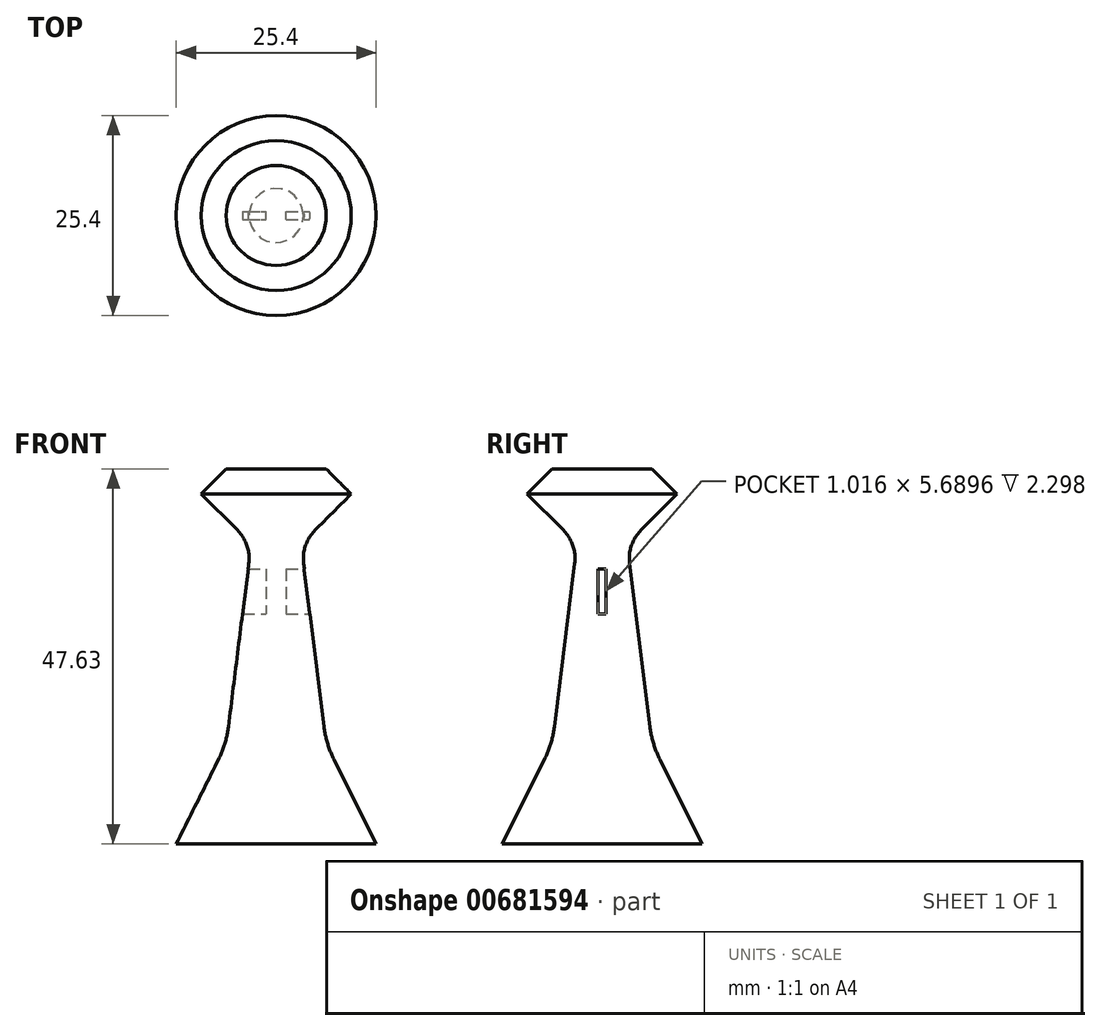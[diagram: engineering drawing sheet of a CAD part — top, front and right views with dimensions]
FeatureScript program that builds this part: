
annotation { "Feature Type Name" : "Feature", "Feature Type Description" : "" }
export const myFeature = defineFeature(function(context is Context, id is Id, definition is map)
    precondition{}
    {
        {
            var Q0;
            Q0=qCreatedBy(makeId("Top.planeOp"),FACE);
            var sketch = newSketch(context, id + "F0", { "sketchPlane" : qUnion([Q0])});
            skCircle(sketch, "E0", {"center": v(0, 0) * mm, "radius": 12.7 * mm});
            skSolve(sketch);
        }
        {
            var Q0;
            Q0=qCreatedBy(makeId("Top.planeOp"),FACE);
            cPlane(context, id + "F1", {"entities" : qUnion([Q0]), "cplaneType" : CPlaneType.OFFSET, "offset" : 12.7 * mm, "width" : 152.4 * mm, "height" : 152.4 * mm});
        }
        {
            var Q0;
            Q0=qCreatedBy(id+"F1.planeOp",FACE);
            var sketch = newSketch(context, id + "F2", { "sketchPlane" : qUnion([Q0])});
            skCircle(sketch, "E1", {"center": v(0, 0) * mm, "radius": 6.35 * mm});
            skSolve(sketch);
        }
        {
            var Q0;
            Q0=makeQuery(id+"F0.imprint","IMPRINT",FACE,{"disambiguationData":[TD([[makeQuery(id+"F0.imprint","IMPRINT",EDGE,{"derivedFrom":sQuery(id+"F0.wireOp",EDGE,"E0")}),1.0]])]});
            var Q1;
            Q1=makeQuery(id+"F2.imprint","IMPRINT",FACE,{"disambiguationData":[TD([[makeQuery(id+"F2.imprint","IMPRINT",EDGE,{"derivedFrom":sQuery(id+"F2.wireOp",EDGE,"E1")}),1.0]])]});
            loft(context, id + "F3", {"sheetProfilesArray" : [{ "sheetProfileEntities" : qUnion([Q0]) }, { "sheetProfileEntities" : qUnion([Q1]) }]});
        }
        {
            var Q0;
            Q0=qCreatedBy(makeId("Top.planeOp"),FACE);
            cPlane(context, id + "F4", {"entities" : qUnion([Q0]), "cplaneType" : CPlaneType.OFFSET, "offset" : 38.1 * mm, "width" : 152.4 * mm, "height" : 152.4 * mm});
        }
        {
            var Q0;
            Q0=qCreatedBy(id+"F4.planeOp",FACE);
            var sketch = newSketch(context, id + "F5", { "sketchPlane" : qUnion([Q0])});
            skCircle(sketch, "E2", {"center": v(0, 0) * mm, "radius": 3.18 * mm});
            skSolve(sketch);
        }
        {
            var Q1;
            Q1=makeQuery(id+"F3.opLoft","CAP_FACE",FACE,{"disambiguationData":[OSD([makeQuery(id+"F2.imprint","IMPRINT",FACE,{"disambiguationData":[TD([[makeQuery(id+"F2.imprint","IMPRINT",EDGE,{"derivedFrom":sQuery(id+"F2.wireOp",EDGE,"E1")}),1.0]])]})])],"isStart":true});
            var Q2;
            Q2=makeQuery(id+"F5.imprint","IMPRINT",FACE,{"disambiguationData":[TD([[makeQuery(id+"F5.imprint","IMPRINT",EDGE,{"derivedFrom":sQuery(id+"F5.wireOp",EDGE,"E2")}),1.0]])]});
            loft(context, id + "F6", {"operationType" : NewBodyOperationType.ADD, "sheetProfilesArray" : [{ "sheetProfileEntities" : qUnion([Q1]) }, { "sheetProfileEntities" : qUnion([Q2]) }]});
        }
        {
            var Q0;
            Q0=qCreatedBy(makeId("Top.planeOp"),FACE);
            cPlane(context, id + "F7", {"entities" : qUnion([Q0]), "cplaneType" : CPlaneType.OFFSET, "offset" : 44.45 * mm, "width" : 152.4 * mm, "height" : 152.4 * mm});
        }
        {
            var Q0;
            Q0=qCreatedBy(id+"F7.planeOp",FACE);
            var sketch = newSketch(context, id + "F8", { "sketchPlane" : qUnion([Q0])});
            skCircle(sketch, "E3", {"center": v(0, 0) * mm, "radius": 9.53 * mm});
            skSolve(sketch);
        }
        {
            var Q1;
            Q1=makeQuery(id+"F6.opLoft","CAP_FACE",FACE,{"disambiguationData":[OSD([makeQuery(id+"F5.imprint","IMPRINT",FACE,{"disambiguationData":[TD([[makeQuery(id+"F5.imprint","IMPRINT",EDGE,{"derivedFrom":sQuery(id+"F5.wireOp",EDGE,"E2")}),1.0]])]})])],"isStart":true});
            var Q2;
            Q2=makeQuery(id+"F8.imprint","IMPRINT",FACE,{"disambiguationData":[TD([[makeQuery(id+"F8.imprint","IMPRINT",EDGE,{"derivedFrom":sQuery(id+"F8.wireOp",EDGE,"E3")}),1.0]])]});
            loft(context, id + "F9", {"operationType" : NewBodyOperationType.ADD, "sheetProfilesArray" : [{ "sheetProfileEntities" : qUnion([Q1]) }, { "sheetProfileEntities" : qUnion([Q2]) }]});
        }
        {
            var Q0;
            {var subQ0=sQuery(id+"F2.wireOp",EDGE,"E1");var subQ1=sQuery(id+"F0.wireOp",EDGE,"E0");Q0=makeQuery(id+"F6.boolean.opBoolean","MERGE",EDGE,{"derivedFrom":[makeQuery(id+"F3.opLoft","MID_CAP_EDGE",EDGE,{"disambiguationData":[OSD([subQ1,subQ0])],"capPos":1.0}),makeQuery(id+"F6.opLoft","MID_CAP_EDGE",EDGE,{"disambiguationData":[OSD([subQ1,subQ0])],"capPos":0.0})]});}
            fillet(context, id + "F10", {"entities" : qUnion([Q0]), "radius" : 12.7 * mm, "tangentPropagation" : true, "allowEdgeOverflow" : false});
        }
        {
            var Q0;
            {var subQ0=sQuery(id+"F5.wireOp",EDGE,"E2");var subQ1=sQuery(id+"F2.wireOp",EDGE,"E1");var subQ2=sQuery(id+"F0.wireOp",EDGE,"E0");Q0=makeQuery(id+"F9.boolean.opBoolean","MERGE",EDGE,{"derivedFrom":[makeQuery(id+"F6.opLoft","MID_CAP_EDGE",EDGE,{"disambiguationData":[OSD([subQ2,subQ1,subQ0])],"capPos":1.0}),makeQuery(id+"F9.opLoft","MID_CAP_EDGE",EDGE,{"disambiguationData":[OSD([subQ2,subQ1,subQ0])],"capPos":0.0})]});}
            fillet(context, id + "F11", {"entities" : qUnion([Q0]), "radius" : 5.08 * mm, "tangentPropagation" : true, "allowEdgeOverflow" : false});
        }
        {
            var Q0;
            Q0=qCreatedBy(makeId("Top.planeOp"),FACE);
            cPlane(context, id + "F12", {"entities" : qUnion([Q0]), "cplaneType" : CPlaneType.OFFSET, "offset" : 46.04 * mm, "width" : 152.4 * mm, "height" : 152.4 * mm});
        }
        {
            var Q0;
            Q0=qCreatedBy(id+"F12.planeOp",FACE);
            var sketch = newSketch(context, id + "F13", { "sketchPlane" : qUnion([Q0])});
            skCircle(sketch, "E4", {"center": v(0, 0) * mm, "radius": 7.94 * mm});
            skSolve(sketch);
        }
        {
            var Q1;
            Q1=makeQuery(id+"F9.opLoft","CAP_FACE",FACE,{"disambiguationData":[OSD([makeQuery(id+"F8.imprint","IMPRINT",FACE,{"disambiguationData":[TD([[makeQuery(id+"F8.imprint","IMPRINT",EDGE,{"derivedFrom":sQuery(id+"F8.wireOp",EDGE,"E3")}),1.0]])]})])],"isStart":true});
            var Q2;
            Q2=makeQuery(id+"F13.imprint","IMPRINT",FACE,{"disambiguationData":[TD([[makeQuery(id+"F13.imprint","IMPRINT",EDGE,{"derivedFrom":sQuery(id+"F13.wireOp",EDGE,"E4")}),1.0]])]});
            loft(context, id + "F14", {"operationType" : NewBodyOperationType.ADD, "sheetProfilesArray" : [{ "sheetProfileEntities" : qUnion([Q1]) }, { "sheetProfileEntities" : qUnion([Q2]) }]});
        }
        {
            var Q0;
            Q0=makeQuery(id+"F14.opLoft","CAP_FACE",FACE,{"disambiguationData":[OSD([makeQuery(id+"F13.imprint","IMPRINT",FACE,{"disambiguationData":[TD([[makeQuery(id+"F13.imprint","IMPRINT",EDGE,{"derivedFrom":sQuery(id+"F13.wireOp",EDGE,"E4")}),1.0]])]})])],"isStart":true});
            cPlane(context, id + "F15", {"entities" : qUnion([Q0]), "cplaneType" : CPlaneType.OFFSET, "offset" : 1.59 * mm, "width" : 152.4 * mm, "height" : 152.4 * mm});
        }
        {
            var Q0;
            Q0=qCreatedBy(id+"F15.planeOp",FACE);
            var sketch = newSketch(context, id + "F16", { "sketchPlane" : qUnion([Q0])});
            skCircle(sketch, "E5", {"center": v(0, 0) * mm, "radius": 6.35 * mm});
            skSolve(sketch);
        }
        {
            var Q1;
            Q1=makeQuery(id+"F16.imprint","IMPRINT",FACE,{"disambiguationData":[TD([[makeQuery(id+"F16.imprint","IMPRINT",EDGE,{"derivedFrom":sQuery(id+"F16.wireOp",EDGE,"E5")}),1.0]])]});
            var Q2;
            Q2=makeQuery(id+"F14.opLoft","CAP_FACE",FACE,{"disambiguationData":[OSD([makeQuery(id+"F13.imprint","IMPRINT",FACE,{"disambiguationData":[TD([[makeQuery(id+"F13.imprint","IMPRINT",EDGE,{"derivedFrom":sQuery(id+"F13.wireOp",EDGE,"E4")}),1.0]])]})])],"isStart":true});
            loft(context, id + "F17", {"operationType" : NewBodyOperationType.ADD, "sheetProfilesArray" : [{ "sheetProfileEntities" : qUnion([Q1]) }, { "sheetProfileEntities" : qUnion([Q2]) }]});
        }
        {
            var Q0;
            Q0=qCreatedBy(makeId("Right.planeOp"),FACE);
            var sketch = newSketch(context, id + "F18", { "sketchPlane" : qUnion([Q0])});
            skLineSegment(sketch, "E6", {"start": v(0, 0) * mm, "end": v(0, 30.16) * mm, "construction": true});
            skLineSegment(sketch, "E7", {"start": v(0, 30.16) * mm, "end": v(0, 34.93) * mm, "construction": true});
            skLineSegment(sketch, "E8.bottom", {"start": v(0, 34.93) * mm, "end": v(0.5, 34.93) * mm});
            skLineSegment(sketch, "E8.top", {"start": v(0, 29.24) * mm, "end": v(0.5, 29.24) * mm});
            skLineSegment(sketch, "E8.left", {"start": v(0, 34.93) * mm, "end": v(0, 29.24) * mm});
            skLineSegment(sketch, "E8.right", {"start": v(0.5, 34.93) * mm, "end": v(0.5, 29.24) * mm});
            skLineSegment(sketch, "E9.bottom", {"start": v(0, 34.93) * mm, "end": v(-0.5, 34.93) * mm});
            skLineSegment(sketch, "E9.top", {"start": v(0, 29.24) * mm, "end": v(-0.5, 29.24) * mm});
            skLineSegment(sketch, "E9.right", {"start": v(-0.5, 34.93) * mm, "end": v(-0.5, 29.24) * mm});
            skSolve(sketch);
        }
        {
            var Q0;
            Q0 = qSketchRegion(id + "F18", true);
            extrude(context, id + "F19", {"entities" : qUnion([Q0]), "operationType" : NewBodyOperationType.REMOVE, "endBound" : BoundingType.THROUGH_ALL, "oppositeDirection" : true, "depth" : 25.4 * mm, "offsetDistance" : 25.4 * mm, "hasSecondDirection" : true, "secondDirectionOppositeDirection" : false, "secondDirectionDepth" : 25.4 * mm});
        }
        {
            var Q0;
            Q0 = qSketchRegion(id + "F18", true);
            extrude(context, id + "F20", {"entities" : qUnion([Q0]), "operationType" : NewBodyOperationType.ADD, "endBound" : BoundingType.SYMMETRIC, "depth" : 2.54 * mm, "offsetDistance" : 25.4 * mm});
        }
    });
